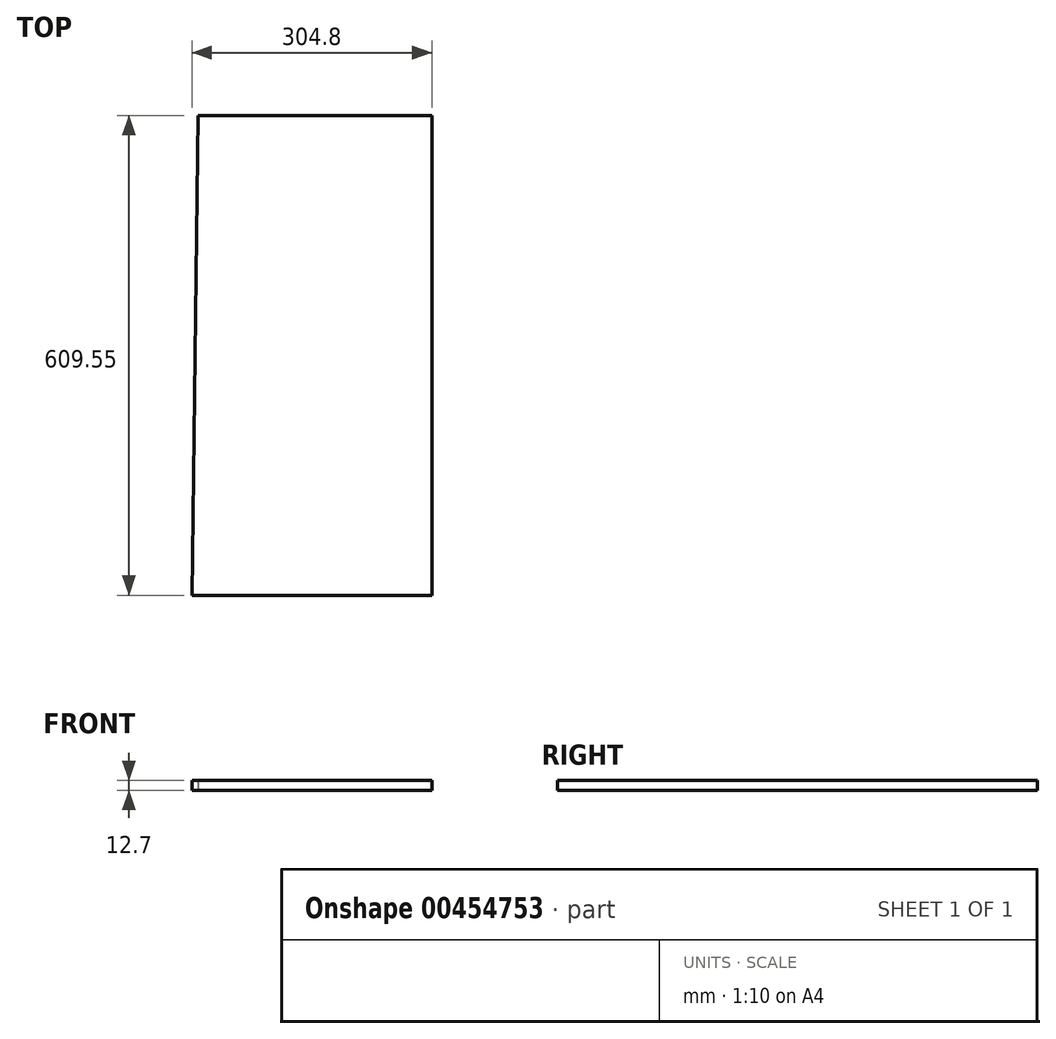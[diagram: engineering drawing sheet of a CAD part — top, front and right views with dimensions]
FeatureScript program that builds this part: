
annotation { "Feature Type Name" : "Feature", "Feature Type Description" : "" }
export const myFeature = defineFeature(function(context is Context, id is Id, definition is map)
    precondition{}
    {
        {
            var Q0;
            Q0=qCreatedBy(makeId("Top.planeOp"),FACE);
            var sketch = newSketch(context, id + "F0", { "sketchPlane" : qUnion([Q0])});
            skLineSegment(sketch, "E0", {"start": v(-148.24, 0) * mm, "end": v(156.56, 0) * mm});
            skLineSegment(sketch, "E1", {"start": v(156.56, 0) * mm, "end": v(156.56, 609.55) * mm});
            skLineSegment(sketch, "E2", {"start": v(156.56, 609.55) * mm, "end": v(-140.6, 609.55) * mm});
            skLineSegment(sketch, "E3", {"start": v(-140.6, 609.55) * mm, "end": v(-148.24, 0) * mm});
            skSolve(sketch);
        }
        {
            var Q0;
            Q0=makeQuery(id+"F0.imprint","IMPRINT",FACE,{"disambiguationData":[TD([[makeQuery(id+"F0.imprint","IMPRINT",EDGE,{"derivedFrom":sQuery(id+"F0.wireOp",EDGE,"E0")}),1.0]])]});
            extrude(context, id + "F1", {"entities" : qUnion([Q0]), "depth" : 12.7 * mm});
        }
    });
